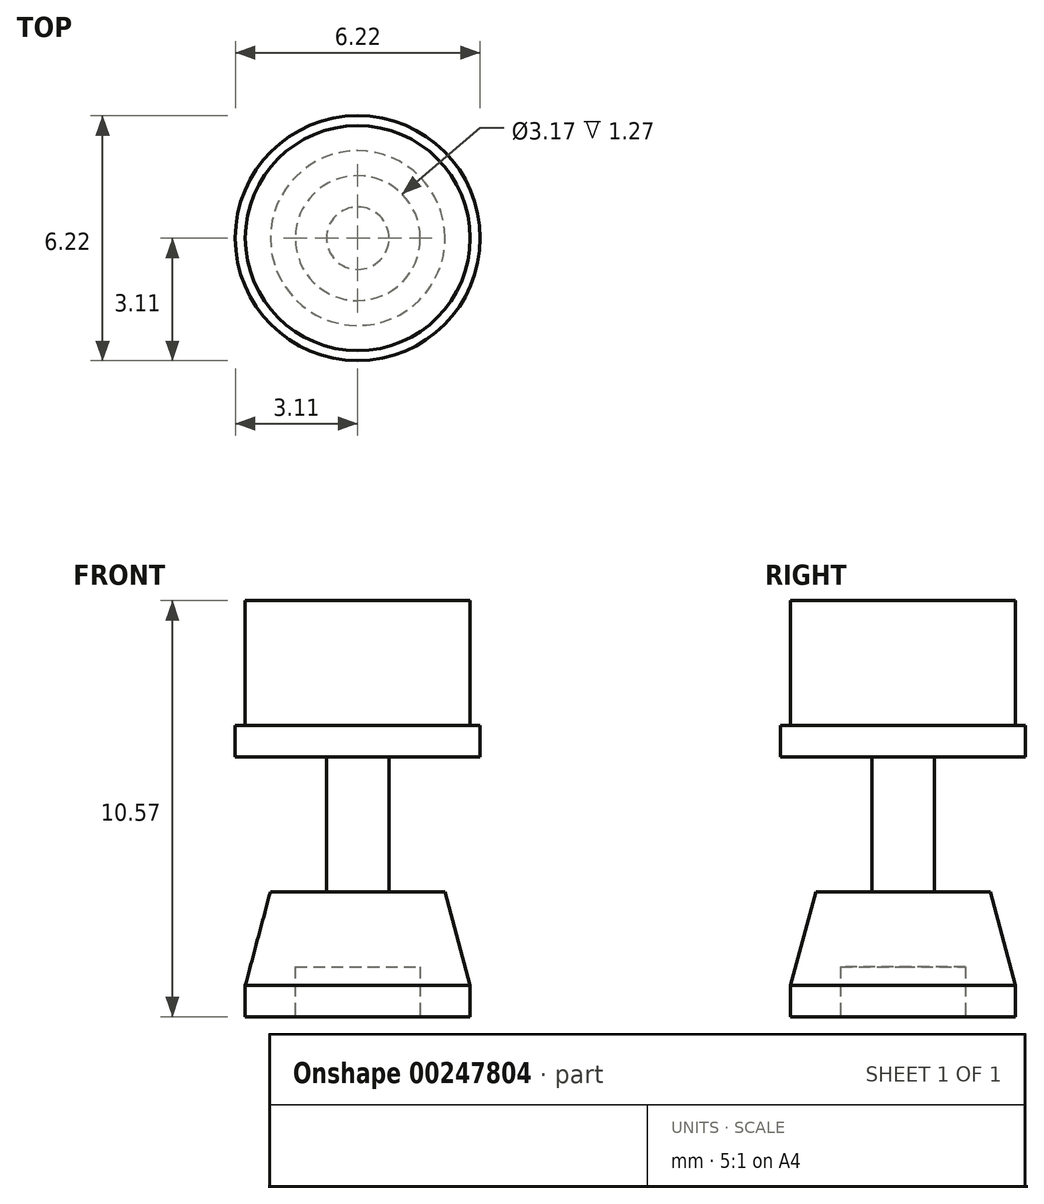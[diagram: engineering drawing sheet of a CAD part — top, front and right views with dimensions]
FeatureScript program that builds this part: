
annotation { "Feature Type Name" : "Feature", "Feature Type Description" : "" }
export const myFeature = defineFeature(function(context is Context, id is Id, definition is map)
    precondition{}
    {
        {
            var Q0;
            Q0=qCreatedBy(makeId("Right.planeOp"),FACE);
            var sketch = newSketch(context, id + "F0", { "sketchPlane" : qUnion([Q0])});
            skLineSegment(sketch, "E0", {"start": v(0, 0) * mm, "end": v(0, 10.57) * mm});
            skLineSegment(sketch, "E1", {"start": v(1.59, 0) * mm, "end": v(2.86, 0) * mm});
            skLineSegment(sketch, "E2", {"start": v(2.86, 0) * mm, "end": v(2.86, 0.8) * mm});
            skLineSegment(sketch, "E3", {"start": v(2.86, 0.8) * mm, "end": v(2.22, 3.18) * mm});
            skLineSegment(sketch, "E4", {"start": v(2.22, 3.17) * mm, "end": v(0.8, 3.17) * mm});
            skLineSegment(sketch, "E5", {"start": v(0.8, 3.18) * mm, "end": v(0.8, 6.6) * mm});
            skLineSegment(sketch, "E6", {"start": v(0.8, 6.6) * mm, "end": v(3.11, 6.6) * mm});
            skLineSegment(sketch, "E7", {"start": v(3.11, 6.6) * mm, "end": v(3.11, 7.4) * mm});
            skLineSegment(sketch, "E8", {"start": v(3.11, 7.4) * mm, "end": v(2.86, 7.4) * mm});
            skLineSegment(sketch, "E9", {"start": v(2.86, 7.4) * mm, "end": v(2.86, 10.57) * mm});
            skLineSegment(sketch, "E10", {"start": v(2.86, 10.57) * mm, "end": v(0, 10.57) * mm});
            skLineSegment(sketch, "E11", {"start": v(0, 10.57) * mm, "end": v(0, 0) * mm, "construction": true});
            skLineSegment(sketch, "E12", {"start": v(0, 1.27) * mm, "end": v(1.59, 1.27) * mm});
            skLineSegment(sketch, "E13", {"start": v(1.59, 1.27) * mm, "end": v(1.59, 0) * mm});
            skSolve(sketch);
        }
        {
            var Q0;
            Q0=makeQuery(id+"F0.imprint","IMPRINT",FACE,{"disambiguationData":[TD([[makeQuery(id+"F0.imprint","IMPRINT",EDGE,{"derivedFrom":sQuery(id+"F0.wireOp",EDGE,"E0")}),-1.0]])]});
            var Q1;
            Q1=sQuery(id+"F0.wireOp",EDGE,"E0");
            revolve(context, id + "F1", {"entities" : qUnion([Q0]), "axis" : qUnion([Q1]), "revolveType" : RevolveType.FULL});
        }
    });
